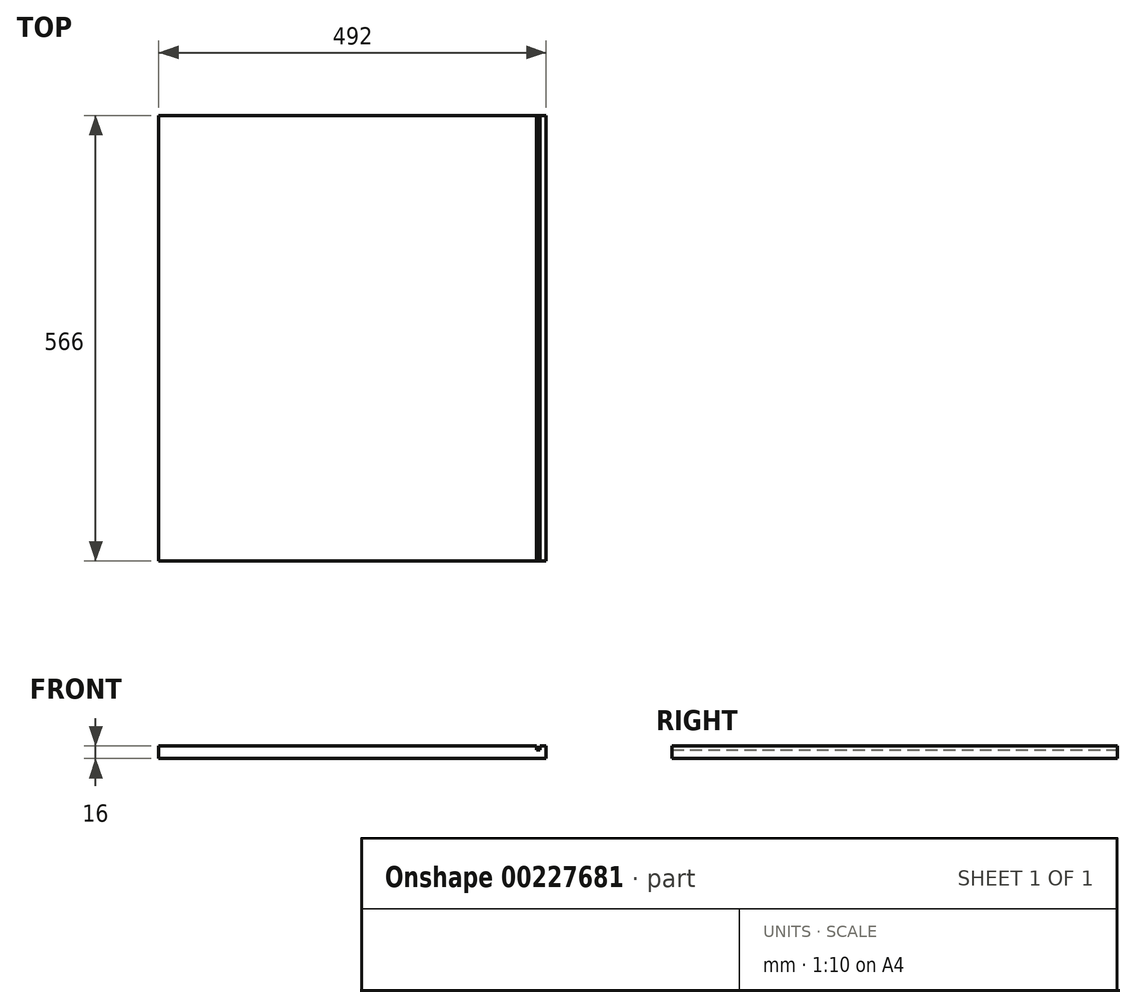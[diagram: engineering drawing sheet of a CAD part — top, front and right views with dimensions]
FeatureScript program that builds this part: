
annotation { "Feature Type Name" : "Feature", "Feature Type Description" : "" }
export const myFeature = defineFeature(function(context is Context, id is Id, definition is map)
    precondition{}
    {
        {
            var Q0;
            Q0=qCreatedBy(makeId("Top.planeOp"),FACE);
            var sketch = newSketch(context, id + "F0", { "sketchPlane" : qUnion([Q0])});
            skLineSegment(sketch, "E0.bottom", {"start": v(246, -283) * mm, "end": v(-246, -283) * mm});
            skLineSegment(sketch, "E0.top", {"start": v(246, 283) * mm, "end": v(-246, 283) * mm});
            skLineSegment(sketch, "E0.left", {"start": v(246, -283) * mm, "end": v(246, 283) * mm});
            skLineSegment(sketch, "E0.right", {"start": v(-246, -283) * mm, "end": v(-246, 283) * mm});
            skPoint(sketch, "E0.middle", {"position": v(0, 0) * mm});
            skSolve(sketch);
        }
        {
            var Q0;
            Q0 = qSketchRegion(id + "F0", true);
            extrude(context, id + "F1", {"entities" : qUnion([Q0]), "depth" : 16 * mm});
        }
        {
            var Q0;
            Q0=makeQuery(id+"F1.opExtrude","SWEPT_FACE",FACE,{"disambiguationData":[OSD([sQuery(id+"F0.wireOp",EDGE,"E0.top")])]});
            var sketch = newSketch(context, id + "F2", { "sketchPlane" : qUnion([Q0])});
            skLineSegment(sketch, "E1.bottom", {"start": v(-238, 16) * mm, "end": v(-234, 16) * mm});
            skLineSegment(sketch, "E1.top", {"start": v(-238, 11) * mm, "end": v(-234, 11) * mm});
            skLineSegment(sketch, "E1.left", {"start": v(-238, 16) * mm, "end": v(-238, 11) * mm});
            skLineSegment(sketch, "E1.right", {"start": v(-234, 16) * mm, "end": v(-234, 11) * mm});
            skSolve(sketch);
        }
        {
            var Q0;
            Q0 = qSketchRegion(id + "F2", true);
            extrude(context, id + "F3", {"entities" : qUnion([Q0]), "operationType" : NewBodyOperationType.REMOVE, "endBound" : BoundingType.THROUGH_ALL, "oppositeDirection" : true, "depth" : 25 * mm});
        }
    });
